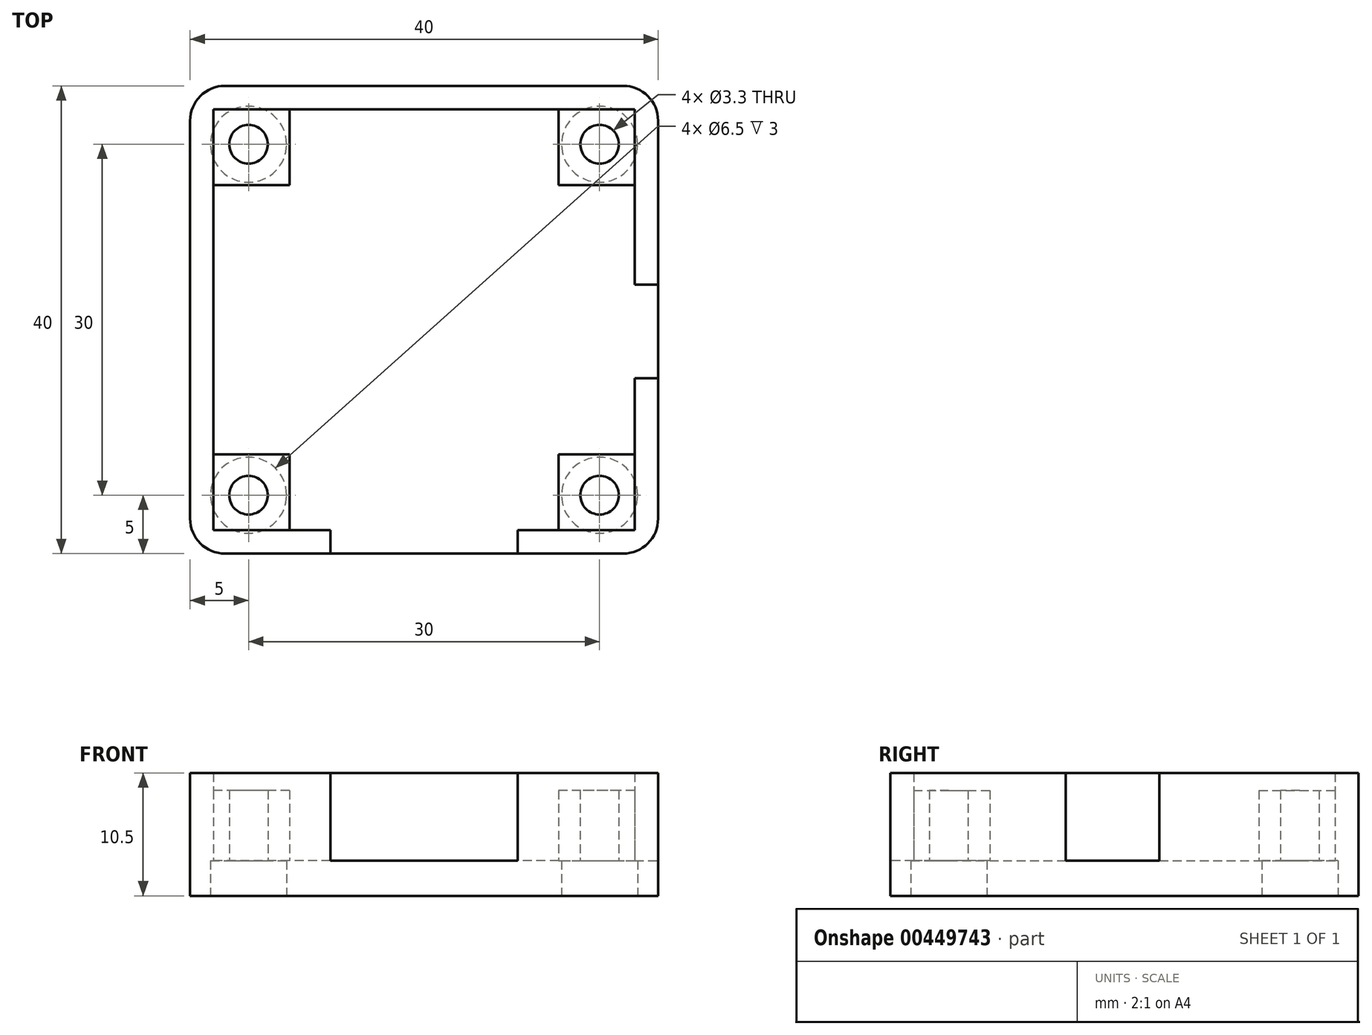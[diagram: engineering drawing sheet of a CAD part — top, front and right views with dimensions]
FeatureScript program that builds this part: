
annotation { "Feature Type Name" : "Feature", "Feature Type Description" : "" }
export const myFeature = defineFeature(function(context is Context, id is Id, definition is map)
    precondition{}
    {
        {
            var Q0;
            Q0=qCreatedBy(makeId("Top.planeOp"),FACE);
            var sketch = newSketch(context, id + "F0", { "sketchPlane" : qUnion([Q0])});
            skLineSegment(sketch, "E0.bottom", {"start": v(18, -18) * mm, "end": v(-18, -18) * mm});
            skLineSegment(sketch, "E0.top", {"start": v(18, 18) * mm, "end": v(-18, 18) * mm});
            skLineSegment(sketch, "E0.left", {"start": v(18, -18) * mm, "end": v(18, 18) * mm});
            skLineSegment(sketch, "E0.right", {"start": v(-18, -18) * mm, "end": v(-18, 18) * mm});
            skPoint(sketch, "E0.middle", {"position": v(0, 0) * mm});
            skLineSegment(sketch, "E1.bottom", {"start": v(15, -15) * mm, "end": v(-15, -15) * mm, "construction": true});
            skLineSegment(sketch, "E1.top", {"start": v(15, 15) * mm, "end": v(-15, 15) * mm, "construction": true});
            skLineSegment(sketch, "E1.left", {"start": v(15, -15) * mm, "end": v(15, 15) * mm, "construction": true});
            skLineSegment(sketch, "E1.right", {"start": v(-15, -15) * mm, "end": v(-15, 15) * mm, "construction": true});
            skLineSegment(sketch, "E2.0", {"start": v(20, 20) * mm, "end": v(-20, 20) * mm});
            skLineSegment(sketch, "E2.1", {"start": v(20, -20) * mm, "end": v(20, 20) * mm});
            skLineSegment(sketch, "E2.2", {"start": v(20, -20) * mm, "end": v(-20, -20) * mm});
            skLineSegment(sketch, "E2.3", {"start": v(-20, -20) * mm, "end": v(-20, 20) * mm});
            skLineSegment(sketch, "E3.bottom", {"start": v(-11.5, 11.5) * mm, "end": v(-18.5, 11.5) * mm});
            skLineSegment(sketch, "E3.left", {"start": v(-11.5, 11.5) * mm, "end": v(-11.5, 18.5) * mm});
            skPoint(sketch, "E3.middle", {"position": v(-15, 15) * mm});
            skLineSegment(sketch, "E4.MirrorCS", {"start": v(11.5, 11.5) * mm, "end": v(11.5, 18.5) * mm});
            skLineSegment(sketch, "E5.MirrorCS", {"start": v(11.5, 11.5) * mm, "end": v(18.5, 11.5) * mm});
            skLineSegment(sketch, "E6.MirrorCS", {"start": v(-11.5, -11.5) * mm, "end": v(-18.5, -11.5) * mm});
            skLineSegment(sketch, "E7.MirrorCS", {"start": v(-11.5, -11.5) * mm, "end": v(-11.5, -18.5) * mm});
            skLineSegment(sketch, "E8.MirrorCS", {"start": v(11.5, -11.5) * mm, "end": v(11.5, -18.5) * mm});
            skLineSegment(sketch, "E9.MirrorCS", {"start": v(11.5, -11.5) * mm, "end": v(18.5, -11.5) * mm});
            skLineSegment(sketch, "E10", {"start": v(-8, -18) * mm, "end": v(-8, -20) * mm});
            skLineSegment(sketch, "E11.MirrorCS", {"start": v(8, -18) * mm, "end": v(8, -20) * mm});
            skLineSegment(sketch, "E12", {"start": v(18, 3) * mm, "end": v(20, 3) * mm});
            skLineSegment(sketch, "E13", {"start": v(18, -5) * mm, "end": v(20, -5) * mm});
            skSolve(sketch);
        }
        {
            var Q0;
            Q0=makeQuery(id+"F0.imprint","IMPRINT",FACE,{"disambiguationData":[TD([[makeQuery(id+"F0.imprint","IMPRINT",EDGE,{"derivedFrom":sQuery(id+"F0.wireOp",EDGE,"E2.0")}),1.0]])]});
            var Q1;
            {var subQ0=sQuery(id+"F0.wireOp",EDGE,"E10");Q1=makeQuery(id+"F0.imprint","IMPRINT",FACE,{"disambiguationData":[TD([[makeQuery(id+"F0.imprint","IMPRINT",EDGE,{"derivedFrom":subQ0}),1.0]])]});}
            var Q2;
            {var subQ4=sQuery(id+"F0.wireOp",EDGE,"E6.MirrorCS");Q2=makeQuery(id+"F0.imprint","IMPRINT",FACE,{"disambiguationData":[TD([[makeQuery(id+"F0.imprint","IMPRINT",EDGE,{"derivedFrom":subQ4}),1.0]])]});}
            var Q3;
            {var subQ1=sQuery(id+"F0.wireOp",EDGE,"E3.bottom");Q3=makeQuery(id+"F0.imprint","IMPRINT",FACE,{"disambiguationData":[TD([[makeQuery(id+"F0.imprint","IMPRINT",EDGE,{"derivedFrom":subQ1}),1.0]])]});}
            var Q4;
            {var subQ3=sQuery(id+"F0.wireOp",EDGE,"E8.MirrorCS");Q4=makeQuery(id+"F0.imprint","IMPRINT",FACE,{"disambiguationData":[TD([[makeQuery(id+"F0.imprint","IMPRINT",EDGE,{"derivedFrom":subQ3}),1.0]])]});}
            var Q5;
            {var subQ3=sQuery(id+"F0.wireOp",EDGE,"E4.MirrorCS");Q5=makeQuery(id+"F0.imprint","IMPRINT",FACE,{"disambiguationData":[TD([[makeQuery(id+"F0.imprint","IMPRINT",EDGE,{"derivedFrom":subQ3}),-1.0]])]});}
            var Q6;
            Q6=makeQuery(id+"F0.imprint","IMPRINT",FACE,{"disambiguationData":[TD([[makeQuery(id+"F0.imprint","IMPRINT",EDGE,{"derivedFrom":sQuery(id+"F0.wireOp",EDGE,"E3.bottom")}),-1.0]])]});
            var Q7;
            {var subQ0=sQuery(id+"F0.wireOp",EDGE,"E12");Q7=makeQuery(id+"F0.imprint","IMPRINT",FACE,{"disambiguationData":[TD([[makeQuery(id+"F0.imprint","IMPRINT",EDGE,{"derivedFrom":subQ0}),-1.0]])]});}
            var Q8;
            {var subQ8=sQuery(id+"F0.wireOp",EDGE,"E11.MirrorCS");Q8=makeQuery(id+"F0.imprint","IMPRINT",FACE,{"disambiguationData":[TD([[makeQuery(id+"F0.imprint","IMPRINT",EDGE,{"derivedFrom":subQ8}),1.0]])]});}
            extrude(context, id + "F1", {"entities" : qUnion([Q0, Q1, Q2, Q3, Q4, Q5, Q6, Q7, Q8]), "oppositeDirection" : true, "depth" : 3 * mm});
        }
        {
            var Q0;
            Q0=makeQuery(id+"F0.imprint","IMPRINT",FACE,{"disambiguationData":[TD([[makeQuery(id+"F0.imprint","IMPRINT",EDGE,{"derivedFrom":sQuery(id+"F0.wireOp",EDGE,"E2.0")}),1.0]])]});
            var Q1;
            {var subQ8=sQuery(id+"F0.wireOp",EDGE,"E11.MirrorCS");Q1=makeQuery(id+"F0.imprint","IMPRINT",FACE,{"disambiguationData":[TD([[makeQuery(id+"F0.imprint","IMPRINT",EDGE,{"derivedFrom":subQ8}),1.0]])]});}
            extrude(context, id + "F2", {"entities" : qUnion([Q0, Q1]), "operationType" : NewBodyOperationType.ADD, "depth" : 7.5 * mm});
        }
        {
            var Q0;
            Q0=makeQuery(id+"F0.imprint","IMPRINT",FACE,{"disambiguationData":[TD([[makeQuery(id+"F0.imprint","IMPRINT",EDGE,{"derivedFrom":sQuery(id+"F0.wireOp",EDGE,"E3.bottom")}),-1.0]])]});
            var Q1;
            {var subQ3=sQuery(id+"F0.wireOp",EDGE,"E4.MirrorCS");Q1=makeQuery(id+"F0.imprint","IMPRINT",FACE,{"disambiguationData":[TD([[makeQuery(id+"F0.imprint","IMPRINT",EDGE,{"derivedFrom":subQ3}),-1.0]])]});}
            var Q2;
            {var subQ3=sQuery(id+"F0.wireOp",EDGE,"E8.MirrorCS");Q2=makeQuery(id+"F0.imprint","IMPRINT",FACE,{"disambiguationData":[TD([[makeQuery(id+"F0.imprint","IMPRINT",EDGE,{"derivedFrom":subQ3}),1.0]])]});}
            var Q3;
            {var subQ4=sQuery(id+"F0.wireOp",EDGE,"E6.MirrorCS");Q3=makeQuery(id+"F0.imprint","IMPRINT",FACE,{"disambiguationData":[TD([[makeQuery(id+"F0.imprint","IMPRINT",EDGE,{"derivedFrom":subQ4}),1.0]])]});}
            extrude(context, id + "F3", {"entities" : qUnion([Q0, Q1, Q2, Q3]), "operationType" : NewBodyOperationType.ADD, "depth" : 6 * mm});
        }
        {
            var Q0;
            Q0=makeQuery(id+"F1.opExtrude","CAP_FACE",FACE,{"disambiguationData":[OSD([sQuery(id+"F0.wireOp",EDGE,"E2.0"),sQuery(id+"F0.wireOp",EDGE,"E2.1"),sQuery(id+"F0.wireOp",EDGE,"E2.2"),sQuery(id+"F0.wireOp",EDGE,"E2.3")])],"isStart":false});
            var sketch = newSketch(context, id + "F4", { "sketchPlane" : qUnion([Q0])});
            skPoint(sketch, "E14.0", {"position": v(-15, 15) * mm});
            skPoint(sketch, "E15.0", {"position": v(-15, -15) * mm});
            skPoint(sketch, "E16.0", {"position": v(15, -15) * mm});
            skPoint(sketch, "E17.0", {"position": v(15, 15) * mm});
            skSolve(sketch);
        }
        {
            var Q0;
            Q0=sQuery(id+"F4.wireOp",VERTEX,"E14.0");
            var Q1;
            Q1=sQuery(id+"F4.wireOp",VERTEX,"E17.0");
            var Q2;
            Q2=sQuery(id+"F4.wireOp",VERTEX,"E16.0");
            var Q3;
            Q3=sQuery(id+"F4.wireOp",VERTEX,"E15.0");
            var Q4;
            Q4=makeQuery(id+"F1.opExtrude","SWEPT_BODY",BODY,{"disambiguationData":[OSD([sQuery(id+"F0.wireOp",EDGE,"E2.0"),sQuery(id+"F0.wireOp",EDGE,"E2.1"),sQuery(id+"F0.wireOp",EDGE,"E2.2"),sQuery(id+"F0.wireOp",EDGE,"E2.3")])]});
            hole(context, id + "F5", {"style" : HoleStyle.C_BORE, "endStyle" : HoleEndStyle.THROUGH, "standardTappedOrClearance" : lookupTablePath({ "standard" : "ISO", "fit" : "Normal", "size" : "M3", "type" : "Clearance" }), "standardBlindInLast" : lookupTablePath({ "fit" : "Standard", "standard" : "ISO", "size" : "M3", "type" : "Clearance" }), "holeDiameter" : 3.3 * mm, "cBoreDiameter" : 6.5 * mm, "cBoreDepth" : 3 * mm, "isTappedThrough" : true, "tappedDepth" : 12 * mm, "tapClearance" : 3, "locations" : qUnion([Q0, Q1, Q2, Q3]), "scope" : qUnion([Q4])});
        }
        {
            var Q0;
            {var subQ0=sQuery(id+"F0.wireOp",EDGE,"E2.3");var subQ1=sQuery(id+"F0.wireOp",EDGE,"E2.2");Q0=makeQuery(id+"F2.boolean.opBoolean","MERGE",EDGE,{"derivedFrom":[makeQuery(id+"F1.opExtrude","SWEPT_EDGE",EDGE,{"disambiguationData":[OSD([subQ1,subQ0])]}),makeQuery(id+"F2.opExtrude","SWEPT_EDGE",EDGE,{"disambiguationData":[OSD([subQ1,subQ0])]})]});}
            var Q1;
            {var subQ0=sQuery(id+"F0.wireOp",EDGE,"E2.2");var subQ1=sQuery(id+"F0.wireOp",EDGE,"E2.1");Q1=makeQuery(id+"F2.boolean.opBoolean","MERGE",EDGE,{"derivedFrom":[makeQuery(id+"F1.opExtrude","SWEPT_EDGE",EDGE,{"disambiguationData":[OSD([subQ1,subQ0])]}),makeQuery(id+"F2.opExtrude","SWEPT_EDGE",EDGE,{"disambiguationData":[OSD([subQ1,subQ0])]})]});}
            var Q2;
            {var subQ0=sQuery(id+"F0.wireOp",EDGE,"E2.3");var subQ1=sQuery(id+"F0.wireOp",EDGE,"E2.0");Q2=makeQuery(id+"F2.boolean.opBoolean","MERGE",EDGE,{"derivedFrom":[makeQuery(id+"F1.opExtrude","SWEPT_EDGE",EDGE,{"disambiguationData":[OSD([subQ1,subQ0])]}),makeQuery(id+"F2.opExtrude","SWEPT_EDGE",EDGE,{"disambiguationData":[OSD([subQ1,subQ0])]})]});}
            var Q3;
            {var subQ0=sQuery(id+"F0.wireOp",EDGE,"E2.1");var subQ1=sQuery(id+"F0.wireOp",EDGE,"E2.0");Q3=makeQuery(id+"F2.boolean.opBoolean","MERGE",EDGE,{"derivedFrom":[makeQuery(id+"F1.opExtrude","SWEPT_EDGE",EDGE,{"disambiguationData":[OSD([subQ1,subQ0])]}),makeQuery(id+"F2.opExtrude","SWEPT_EDGE",EDGE,{"disambiguationData":[OSD([subQ1,subQ0])]})]});}
            var Q4;
            Q4=makeQuery(id+"F2.opExtrude","CAP_EDGE",EDGE,{"disambiguationData":[OSD([sQuery(id+"F0.wireOp",EDGE,"E10")])],"isStart":true});
            var Q5;
            Q5=makeQuery(id+"F2.opExtrude","CAP_EDGE",EDGE,{"disambiguationData":[OSD([sQuery(id+"F0.wireOp",EDGE,"E11.MirrorCS")])],"isStart":true});
            var Q6;
            Q6=makeQuery(id+"F2.opExtrude","CAP_EDGE",EDGE,{"disambiguationData":[OSD([sQuery(id+"F0.wireOp",EDGE,"E12")])],"isStart":true});
            var Q7;
            Q7=makeQuery(id+"F2.opExtrude","CAP_EDGE",EDGE,{"disambiguationData":[OSD([sQuery(id+"F0.wireOp",EDGE,"E13")])],"isStart":true});
            fillet(context, id + "F6", {"entities" : qUnion([Q0, Q1, Q2, Q3, Q4, Q5, Q6, Q7]), "radius" : 3 * mm, "tangentPropagation" : true, "allowEdgeOverflow" : false});
        }
    });
